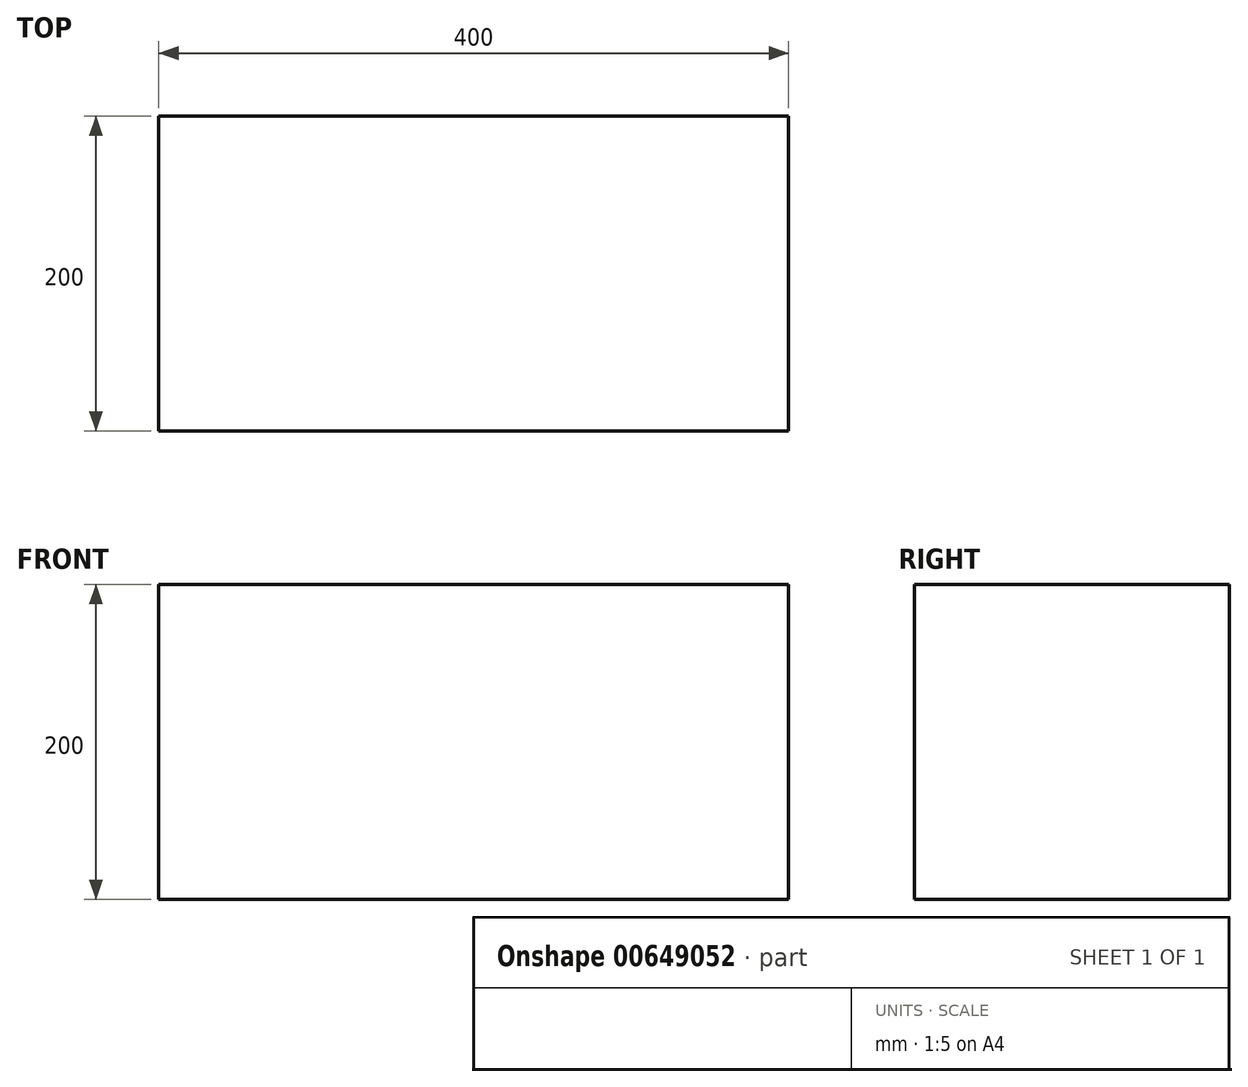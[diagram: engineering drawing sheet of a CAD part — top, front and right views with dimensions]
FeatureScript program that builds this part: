
annotation { "Feature Type Name" : "Feature", "Feature Type Description" : "" }
export const myFeature = defineFeature(function(context is Context, id is Id, definition is map)
    precondition{}
    {
        {
            var Q0;
            Q0=qCreatedBy(makeId("Front.planeOp"),FACE);
            var sketch = newSketch(context, id + "F0", { "sketchPlane" : qUnion([Q0])});
            skLineSegment(sketch, "E0.bottom", {"start": v(-212.67, 92.56) * mm, "end": v(187.33, 92.56) * mm});
            skLineSegment(sketch, "E0.top", {"start": v(-212.67, -107.44) * mm, "end": v(187.33, -107.44) * mm});
            skLineSegment(sketch, "E0.left", {"start": v(-212.67, 92.56) * mm, "end": v(-212.67, -107.44) * mm});
            skLineSegment(sketch, "E0.right", {"start": v(187.33, 92.56) * mm, "end": v(187.33, -107.44) * mm});
            skSolve(sketch);
        }
        {
            var Q0;
            Q0=makeQuery(id+"F0.imprint","IMPRINT",FACE,{"disambiguationData":[TD([[makeQuery(id+"F0.imprint","IMPRINT",EDGE,{"derivedFrom":sQuery(id+"F0.wireOp",EDGE,"E0.bottom")}),-1.0]])]});
            extrude(context, id + "F1", {"entities" : qUnion([Q0]), "depth" : 200 * mm, "offsetDistance" : 25 * mm});
        }
    });
